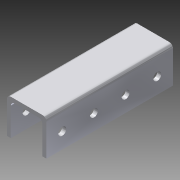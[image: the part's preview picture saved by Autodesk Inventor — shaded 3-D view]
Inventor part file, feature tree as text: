
AUTODESK INVENTOR PART (.ipt)
format: ipt  version: 2015 (Build 190159000, 159)  size: 400,896 bytes
history: native  units: in
note: dims shown in document units (in); Inventor stores cm internally (conversion verified against a paired STEP export)
features: extrude x2, sketch x2, pattern_linear x1
ambient origin geometry x8: Origin, YZ Plane, XZ Plane, XY Plane, X Axis, Y Axis, Z Axis, Center Point
bodies: Solid1 (feature_tree)
feature tree (5):
  extrude  "Extrusion1"  Depth=4.0in
  extrude  "Extrusion4"  Depth=0.5in
  pattern_linear  "Rectangular Pattern3"  Spacing1=0.5in  [1 undecoded]
  sketch  "Sketch1"  dims[d0=1.13in d1=1.25in d2=0.125in d3=0.125in d4=0.125in d5=4.0in]
  sketch  "Sketch4"  dims[d6=0.0in d34=0.5in d35=0.5in d36=0.25in d37=1.0in d38=0.0in d39=11.811in d41=1.0in d42=11.811in d44=1.0in]
note: 1 required parameter value undecoded (feature->parameter linkage not recoverable at this tier; creation-order binding heuristic only, values carry confidence <= 0.55)
